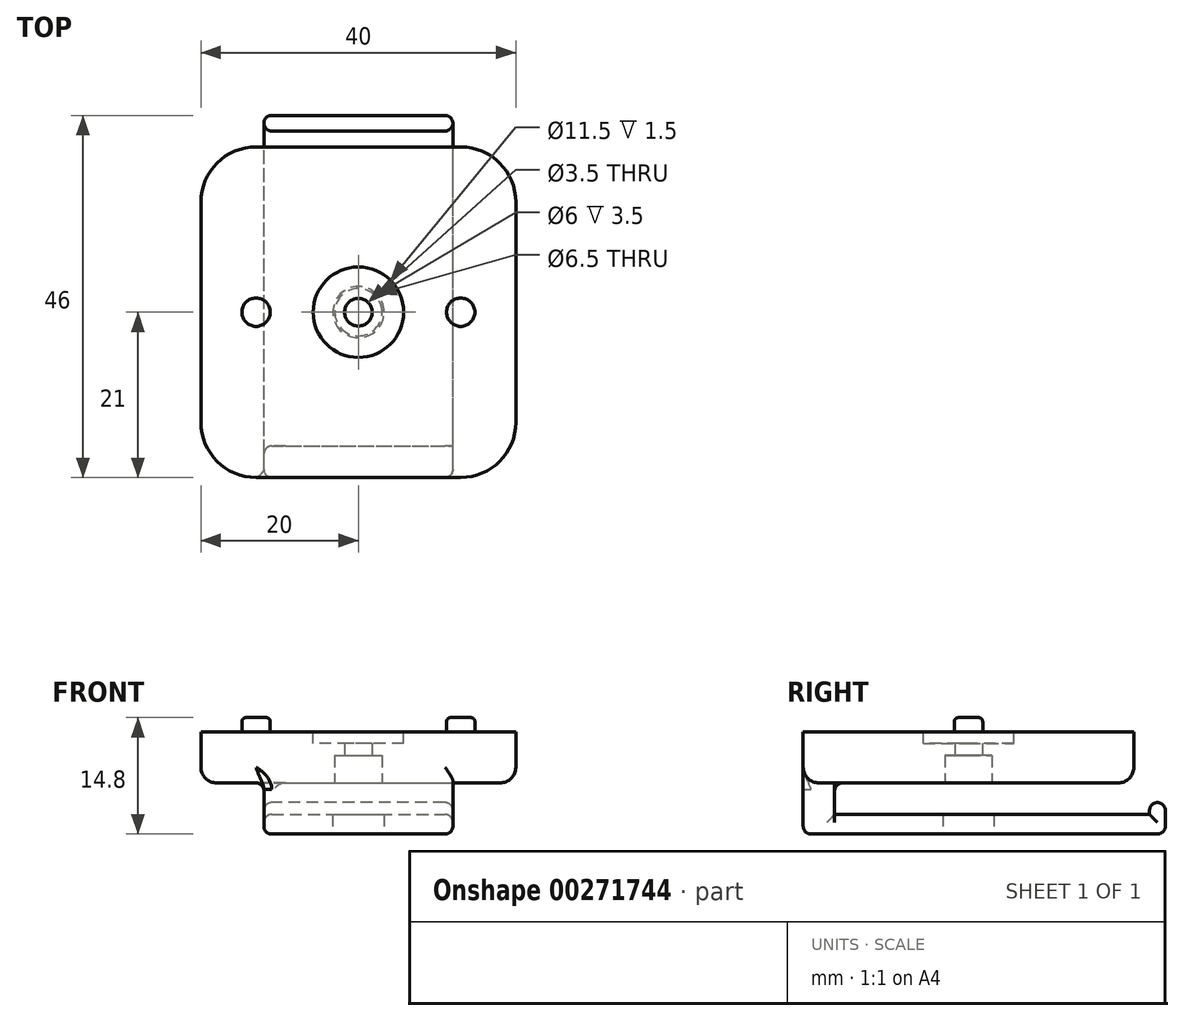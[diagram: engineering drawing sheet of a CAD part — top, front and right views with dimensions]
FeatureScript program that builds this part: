
annotation { "Feature Type Name" : "Feature", "Feature Type Description" : "" }
export const myFeature = defineFeature(function(context is Context, id is Id, definition is map)
    precondition{}
    {
        {
            var Q0;
            Q0=qCreatedBy(makeId("Top.planeOp"),FACE);
            var sketch = newSketch(context, id + "F0", { "sketchPlane" : qUnion([Q0])});
            skLineSegment(sketch, "E0.bottom", {"start": v(-20, 21) * mm, "end": v(20, 21) * mm});
            skLineSegment(sketch, "E0.top", {"start": v(-20, -21) * mm, "end": v(20, -21) * mm});
            skLineSegment(sketch, "E0.left", {"start": v(-20, 21) * mm, "end": v(-20, -21) * mm});
            skLineSegment(sketch, "E0.right", {"start": v(20, 21) * mm, "end": v(20, -21) * mm});
            skSolve(sketch);
        }
        {
            var Q0;
            Q0 = qSketchRegion(id + "F0", true);
            extrude(context, id + "F1", {"entities" : qUnion([Q0]), "depth" : 6.5 * mm});
        }
        {
            var Q0;
            Q0=makeQuery(id+"F1.opExtrude","CAP_FACE",FACE,{"disambiguationData":[OSD([sQuery(id+"F0.wireOp",EDGE,"E0.bottom"),sQuery(id+"F0.wireOp",EDGE,"E0.top"),sQuery(id+"F0.wireOp",EDGE,"E0.left"),sQuery(id+"F0.wireOp",EDGE,"E0.right")])],"isStart":false});
            var sketch = newSketch(context, id + "F2", { "sketchPlane" : qUnion([Q0])});
            skCircle(sketch, "E1", {"center": v(0, 0) * mm, "radius": 5.75 * mm});
            skSolve(sketch);
        }
        {
            var Q0;
            Q0 = qSketchRegion(id + "F2", true);
            extrude(context, id + "F3", {"entities" : qUnion([Q0]), "operationType" : NewBodyOperationType.REMOVE, "oppositeDirection" : true, "depth" : 1.5 * mm});
        }
        {
            var Q0;
            Q0=makeQuery(id+"F1.opExtrude","CAP_FACE",FACE,{"disambiguationData":[OSD([sQuery(id+"F0.wireOp",EDGE,"E0.bottom"),sQuery(id+"F0.wireOp",EDGE,"E0.top"),sQuery(id+"F0.wireOp",EDGE,"E0.left"),sQuery(id+"F0.wireOp",EDGE,"E0.right")])],"isStart":false});
            var sketch = newSketch(context, id + "F4", { "sketchPlane" : qUnion([Q0])});
            skCircle(sketch, "E2", {"center": v(13, 0) * mm, "radius": 1.8 * mm});
            skCircle(sketch, "E3", {"center": v(-13, 0) * mm, "radius": 1.8 * mm});
            skSolve(sketch);
        }
        {
            var Q0;
            Q0 = qSketchRegion(id + "F4", true);
            extrude(context, id + "F5", {"entities" : qUnion([Q0]), "operationType" : NewBodyOperationType.ADD, "depth" : 1.8 * mm});
        }
        {
            var Q0;
            Q0=makeQuery(id+"F1.opExtrude","CAP_FACE",FACE,{"disambiguationData":[OSD([sQuery(id+"F0.wireOp",EDGE,"E0.bottom"),sQuery(id+"F0.wireOp",EDGE,"E0.top"),sQuery(id+"F0.wireOp",EDGE,"E0.left"),sQuery(id+"F0.wireOp",EDGE,"E0.right")])],"isStart":true});
            var sketch = newSketch(context, id + "F6", { "sketchPlane" : qUnion([Q0])});
            skPoint(sketch, "E4", {"position": v(0, 0) * mm});
            skSolve(sketch);
        }
        {
            var Q0;
            Q0=sQuery(id+"F6.wireOp",VERTEX,"E4");
            var Q1;
            Q1=makeQuery(id+"F1.opExtrude","SWEPT_BODY",BODY,{"disambiguationData":[OSD([sQuery(id+"F0.wireOp",EDGE,"E0.bottom"),sQuery(id+"F0.wireOp",EDGE,"E0.top"),sQuery(id+"F0.wireOp",EDGE,"E0.left"),sQuery(id+"F0.wireOp",EDGE,"E0.right")])]});
            hole(context, id + "F7", {"style" : HoleStyle.C_BORE, "endStyle" : HoleEndStyle.BLIND, "holeDiameter" : 3.5 * mm, "cBoreDiameter" : 6 * mm, "cBoreDepth" : 3.5 * mm, "holeDepth" : 10 * mm, "isTappedThrough" : true, "tappedDepth" : 12 * mm, "tapClearance" : 3, "startFromSketch" : true, "locations" : qUnion([Q0]), "scope" : qUnion([Q1])});
        }
        {
            var Q0;
            Q0=makeQuery(id+"F1.opExtrude","CAP_FACE",FACE,{"disambiguationData":[OSD([sQuery(id+"F0.wireOp",EDGE,"E0.bottom"),sQuery(id+"F0.wireOp",EDGE,"E0.top"),sQuery(id+"F0.wireOp",EDGE,"E0.left"),sQuery(id+"F0.wireOp",EDGE,"E0.right")])],"isStart":true});
            var sketch = newSketch(context, id + "F8", { "sketchPlane" : qUnion([Q0])});
            skLineSegment(sketch, "E5.bottom", {"start": v(-12, 21) * mm, "end": v(12, 21) * mm});
            skLineSegment(sketch, "E5.top", {"start": v(-12, 17) * mm, "end": v(12, 17) * mm});
            skLineSegment(sketch, "E5.left", {"start": v(-12, 21) * mm, "end": v(-12, 17) * mm});
            skLineSegment(sketch, "E5.right", {"start": v(12, 21) * mm, "end": v(12, 17) * mm});
            skSolve(sketch);
        }
        {
            var Q0;
            Q0 = qSketchRegion(id + "F8", true);
            extrude(context, id + "F9", {"entities" : qUnion([Q0]), "operationType" : NewBodyOperationType.ADD, "depth" : 4 * mm});
        }
        {
            var Q0;
            Q0=makeQuery(id+"F9.opExtrude","CAP_FACE",FACE,{"disambiguationData":[OSD([sQuery(id+"F8.wireOp",EDGE,"E5.bottom"),sQuery(id+"F8.wireOp",EDGE,"E5.top"),sQuery(id+"F8.wireOp",EDGE,"E5.left"),sQuery(id+"F8.wireOp",EDGE,"E5.right")])],"isStart":false});
            var sketch = newSketch(context, id + "F10", { "sketchPlane" : qUnion([Q0])});
            skLineSegment(sketch, "E6.bottom", {"start": v(-12, 21) * mm, "end": v(12, 21) * mm});
            skLineSegment(sketch, "E6.top", {"start": v(-12, -23) * mm, "end": v(12, -23) * mm});
            skLineSegment(sketch, "E6.left", {"start": v(-12, 21) * mm, "end": v(-12, -23) * mm});
            skLineSegment(sketch, "E6.right", {"start": v(12, 21) * mm, "end": v(12, -23) * mm});
            skSolve(sketch);
        }
        {
            var Q0;
            Q0 = qSketchRegion(id + "F10", true);
            extrude(context, id + "F11", {"entities" : qUnion([Q0]), "operationType" : NewBodyOperationType.ADD, "depth" : 2.5 * mm});
        }
        {
            var Q0;
            Q0=makeQuery(id+"F11.opExtrude","SWEPT_FACE",FACE,{"disambiguationData":[OSD([sQuery(id+"F10.wireOp",EDGE,"E6.top")])]});
            var sketch = newSketch(context, id + "F12", { "sketchPlane" : qUnion([Q0])});
            skLineSegment(sketch, "E7.bottom", {"start": v(-12, -6.5) * mm, "end": v(12, -6.5) * mm});
            skLineSegment(sketch, "E7.top", {"start": v(-12, -2.5) * mm, "end": v(12, -2.5) * mm});
            skLineSegment(sketch, "E7.left", {"start": v(-12, -6.5) * mm, "end": v(-12, -2.5) * mm});
            skLineSegment(sketch, "E7.right", {"start": v(12, -6.5) * mm, "end": v(12, -2.5) * mm});
            skSolve(sketch);
        }
        {
            var Q0;
            Q0 = qSketchRegion(id + "F12", true);
            extrude(context, id + "F13", {"entities" : qUnion([Q0]), "operationType" : NewBodyOperationType.ADD, "depth" : 2 * mm});
        }
        {
            var Q0;
            Q0=makeQuery(id+"F13.boolean.opBoolean","MERGE",FACE,{"derivedFrom":[makeQuery(id+"F11.opExtrude","CAP_FACE",FACE,{"disambiguationData":[OSD([sQuery(id+"F10.wireOp",EDGE,"E6.bottom"),sQuery(id+"F10.wireOp",EDGE,"E6.top"),sQuery(id+"F10.wireOp",EDGE,"E6.left"),sQuery(id+"F10.wireOp",EDGE,"E6.right")])],"isStart":false}),makeQuery(id+"F13.opExtrude","SWEPT_FACE",FACE,{"disambiguationData":[OSD([sQuery(id+"F12.wireOp",EDGE,"E7.bottom")])]})]});
            var sketch = newSketch(context, id + "F14", { "sketchPlane" : qUnion([Q0])});
            skCircle(sketch, "E8", {"center": v(0, 0) * mm, "radius": 3.25 * mm});
            skSolve(sketch);
        }
        {
            var Q0;
            Q0 = qSketchRegion(id + "F14", true);
            extrude(context, id + "F15", {"entities" : qUnion([Q0]), "operationType" : NewBodyOperationType.REMOVE, "oppositeDirection" : true, "depth" : 2.5 * mm});
        }
        {
            var Q0;
            Q0=makeQuery(id+"F1.opExtrude","SWEPT_EDGE",EDGE,{"disambiguationData":[OSD([sQuery(id+"F0.wireOp",EDGE,"E0.top"),sQuery(id+"F0.wireOp",EDGE,"E0.right")])]});
            var Q1;
            Q1=makeQuery(id+"F1.opExtrude","SWEPT_EDGE",EDGE,{"disambiguationData":[OSD([sQuery(id+"F0.wireOp",EDGE,"E0.top"),sQuery(id+"F0.wireOp",EDGE,"E0.left")])]});
            var Q2;
            Q2=makeQuery(id+"F1.opExtrude","SWEPT_EDGE",EDGE,{"disambiguationData":[OSD([sQuery(id+"F0.wireOp",EDGE,"E0.bottom"),sQuery(id+"F0.wireOp",EDGE,"E0.left")])]});
            var Q3;
            Q3=makeQuery(id+"F1.opExtrude","SWEPT_EDGE",EDGE,{"disambiguationData":[OSD([sQuery(id+"F0.wireOp",EDGE,"E0.bottom"),sQuery(id+"F0.wireOp",EDGE,"E0.right")])]});
            fillet(context, id + "F16", {"entities" : qUnion([Q0, Q1, Q2, Q3]), "radius" : 7 * mm, "tangentPropagation" : true, "allowEdgeOverflow" : false});
        }
        {
            var Q0;
            Q0=makeQuery(id+"F1.opExtrude","CAP_EDGE",EDGE,{"disambiguationData":[OSD([sQuery(id+"F0.wireOp",EDGE,"E0.right")])],"isStart":true});
            fillet(context, id + "F17", {"entities" : qUnion([Q0]), "radius" : 2 * mm, "tangentPropagation" : true, "allowEdgeOverflow" : false});
        }
        {
            var Q0;
            Q0=makeQuery(id+"F13.opExtrude","CAP_EDGE",EDGE,{"disambiguationData":[OSD([sQuery(id+"F12.wireOp",EDGE,"E7.top")])],"isStart":false});
            var Q1;
            Q1=makeQuery(id+"F13.opExtrude","CAP_EDGE",EDGE,{"disambiguationData":[OSD([sQuery(id+"F12.wireOp",EDGE,"E7.top")])],"isStart":true});
            var Q2;
            Q2=makeQuery(id+"F13.opExtrude","SWEPT_EDGE",EDGE,{"disambiguationData":[OSD([sQuery(id+"F12.wireOp",EDGE,"E7.top"),sQuery(id+"F12.wireOp",EDGE,"E7.left")])]});
            var Q3;
            Q3=makeQuery(id+"F13.opExtrude","SWEPT_EDGE",EDGE,{"disambiguationData":[OSD([sQuery(id+"F12.wireOp",EDGE,"E7.top"),sQuery(id+"F12.wireOp",EDGE,"E7.right")])]});
            var Q4;
            Q4=makeQuery(id+"F13.opExtrude","CAP_EDGE",EDGE,{"disambiguationData":[OSD([sQuery(id+"F12.wireOp",EDGE,"E7.right")])],"isStart":false});
            var Q5;
            Q5=makeQuery(id+"F13.opExtrude","CAP_EDGE",EDGE,{"disambiguationData":[OSD([sQuery(id+"F12.wireOp",EDGE,"E7.bottom")])],"isStart":false});
            var Q6;
            Q6=makeQuery(id+"F13.boolean.opBoolean","MERGE",EDGE,{"derivedFrom":[makeQuery(id+"F11.opExtrude","CAP_EDGE",EDGE,{"disambiguationData":[OSD([sQuery(id+"F10.wireOp",EDGE,"E6.right")])],"isStart":false}),makeQuery(id+"F13.opExtrude","SWEPT_EDGE",EDGE,{"disambiguationData":[OSD([sQuery(id+"F12.wireOp",EDGE,"E7.bottom"),sQuery(id+"F12.wireOp",EDGE,"E7.left")])]})]});
            var Q7;
            Q7=makeQuery(id+"F13.opExtrude","CAP_EDGE",EDGE,{"disambiguationData":[OSD([sQuery(id+"F12.wireOp",EDGE,"E7.left")])],"isStart":false});
            var Q8;
            Q8=makeQuery(id+"F13.boolean.opBoolean","MERGE",EDGE,{"derivedFrom":[makeQuery(id+"F11.opExtrude","CAP_EDGE",EDGE,{"disambiguationData":[OSD([sQuery(id+"F10.wireOp",EDGE,"E6.left")])],"isStart":false}),makeQuery(id+"F13.opExtrude","SWEPT_EDGE",EDGE,{"disambiguationData":[OSD([sQuery(id+"F12.wireOp",EDGE,"E7.bottom"),sQuery(id+"F12.wireOp",EDGE,"E7.right")])]})]});
            var Q9;
            Q9=makeQuery(id+"F11.opExtrude","CAP_EDGE",EDGE,{"disambiguationData":[OSD([sQuery(id+"F10.wireOp",EDGE,"E6.bottom")])],"isStart":false});
            var Q10;
            Q10=makeQuery(id+"F11.boolean.opBoolean","MERGE",EDGE,{"derivedFrom":[makeQuery(id+"F9.opExtrude","SWEPT_EDGE",EDGE,{"disambiguationData":[OSD([sQuery(id+"F0.wireOp",EDGE,"E0.top"),sQuery(id+"F8.wireOp",EDGE,"E5.bottom"),sQuery(id+"F8.wireOp",EDGE,"E5.left")])]}),makeQuery(id+"F11.opExtrude","SWEPT_EDGE",EDGE,{"disambiguationData":[OSD([sQuery(id+"F10.wireOp",EDGE,"E6.bottom"),sQuery(id+"F10.wireOp",EDGE,"E6.left")])]})]});
            var Q11;
            Q11=makeQuery(id+"F11.boolean.opBoolean","MERGE",EDGE,{"derivedFrom":[makeQuery(id+"F9.opExtrude","SWEPT_EDGE",EDGE,{"disambiguationData":[OSD([sQuery(id+"F0.wireOp",EDGE,"E0.top"),sQuery(id+"F8.wireOp",EDGE,"E5.bottom"),sQuery(id+"F8.wireOp",EDGE,"E5.right")])]}),makeQuery(id+"F11.opExtrude","SWEPT_EDGE",EDGE,{"disambiguationData":[OSD([sQuery(id+"F10.wireOp",EDGE,"E6.bottom"),sQuery(id+"F10.wireOp",EDGE,"E6.right")])]})]});
            var Q12;
            Q12=makeQuery(id+"F9.opExtrude","CAP_EDGE",EDGE,{"disambiguationData":[OSD([sQuery(id+"F8.wireOp",EDGE,"E5.left")])],"isStart":true});
            var Q13;
            Q13=makeQuery(id+"F9.opExtrude","CAP_EDGE",EDGE,{"disambiguationData":[OSD([sQuery(id+"F8.wireOp",EDGE,"E5.top")])],"isStart":true});
            var Q14;
            Q14=makeQuery(id+"F9.opExtrude","CAP_EDGE",EDGE,{"disambiguationData":[OSD([sQuery(id+"F8.wireOp",EDGE,"E5.top")])],"isStart":false});
            var Q15;
            Q15=makeQuery(id+"F11.opExtrude","CAP_EDGE",EDGE,{"disambiguationData":[OSD([sQuery(id+"F10.wireOp",EDGE,"E6.left")])],"isStart":true});
            var Q16;
            Q16=makeQuery(id+"F13.boolean.opBoolean","MERGE",FACE,{"derivedFrom":[makeQuery(id+"F11.boolean.opBoolean","MERGE",FACE,{"derivedFrom":[makeQuery(id+"F9.opExtrude","SWEPT_FACE",FACE,{"disambiguationData":[OSD([sQuery(id+"F8.wireOp",EDGE,"E5.left")])]}),makeQuery(id+"F11.opExtrude","SWEPT_FACE",FACE,{"disambiguationData":[OSD([sQuery(id+"F10.wireOp",EDGE,"E6.left")])]})]}),makeQuery(id+"F13.opExtrude","SWEPT_FACE",FACE,{"disambiguationData":[OSD([sQuery(id+"F12.wireOp",EDGE,"E7.right")])]})]});
            var Q17;
            Q17=makeQuery(id+"F13.opExtrude","CAP_EDGE",EDGE,{"disambiguationData":[OSD([sQuery(id+"F12.wireOp",EDGE,"E7.left")])],"isStart":true});
            var Q18;
            Q18=makeQuery(id+"F11.opExtrude","CAP_EDGE",EDGE,{"disambiguationData":[OSD([sQuery(id+"F10.wireOp",EDGE,"E6.right")])],"isStart":true});
            var Q19;
            Q19=makeQuery(id+"F15.boolean.opBoolean","COPY",EDGE,{"derivedFrom":makeQuery(id+"F15.opExtrude","CAP_EDGE",EDGE,{"disambiguationData":[OSD([sQuery(id+"F14.wireOp",EDGE,"E8")])],"isStart":true})});
            var Q20;
            Q20=makeQuery(id+"F15.boolean.opBoolean","COPY",EDGE,{"derivedFrom":makeQuery(id+"F15.opExtrude","CAP_EDGE",EDGE,{"disambiguationData":[OSD([sQuery(id+"F14.wireOp",EDGE,"E8")])],"isStart":false})});
            fillet(context, id + "F18", {"entities" : qUnion([Q0, Q1, Q2, Q3, Q4, Q5, Q6, Q7, Q8, Q9, Q10, Q11, Q12, Q13, Q14, Q15, Q16, Q17, Q18, Q19, Q20]), "radius" : 1 * mm, "tangentPropagation" : true, "allowEdgeOverflow" : false});
        }
        {
            var Q0;
            Q0=makeQuery(id+"F5.opExtrude","CAP_EDGE",EDGE,{"disambiguationData":[OSD([sQuery(id+"F4.wireOp",EDGE,"E3")])],"isStart":false});
            var Q1;
            Q1=makeQuery(id+"F5.opExtrude","CAP_EDGE",EDGE,{"disambiguationData":[OSD([sQuery(id+"F4.wireOp",EDGE,"E2")])],"isStart":false});
            fillet(context, id + "F19", {"entities" : qUnion([Q0, Q1]), "radius" : .5 * mm, "tangentPropagation" : true, "allowEdgeOverflow" : false});
        }
    });
